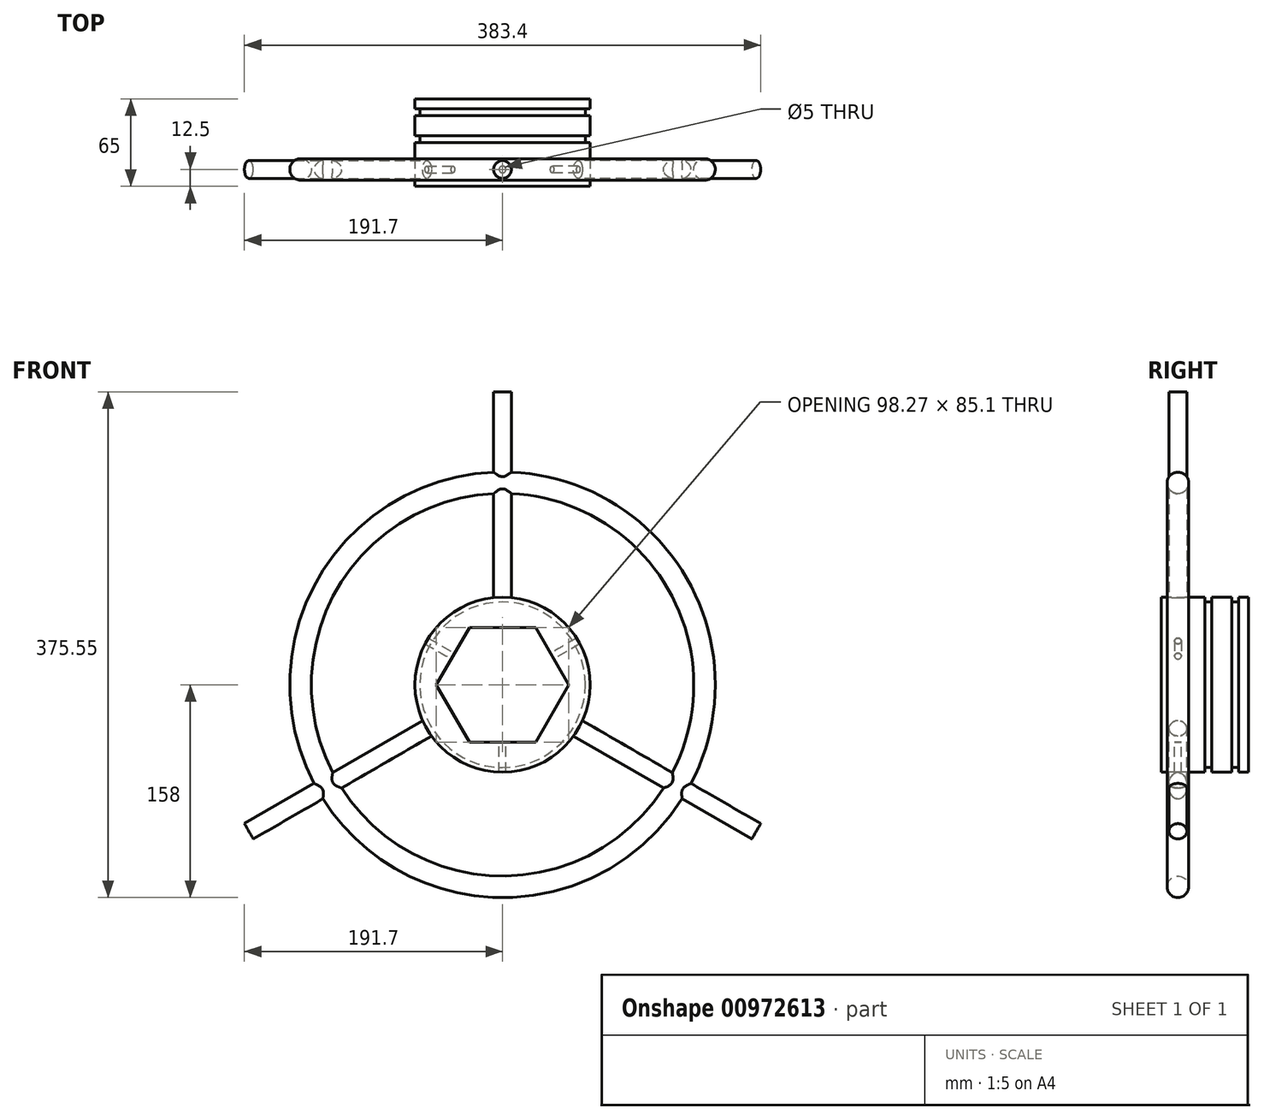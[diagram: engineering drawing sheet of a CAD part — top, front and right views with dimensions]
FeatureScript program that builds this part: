
annotation { "Feature Type Name" : "Feature", "Feature Type Description" : "" }
export const myFeature = defineFeature(function(context is Context, id is Id, definition is map)
    precondition{}
    {
        {
            var Q0;
            Q0=qCreatedBy(makeId("Front.planeOp"),FACE);
            var sketch = newSketch(context, id + "F0", { "sketchPlane" : qUnion([Q0])});
            skArc(sketch, "E0.cCircle", {"start": v(21.28, 36.85) * mm, "mid": v(-21.27, 36.85) * mm, "end": v(-42.55, 0) * mm, "construction": true});
            skLineSegment(sketch, "E0.0", {"start": v(-24.57, 42.55) * mm, "end": v(24.57, 42.55) * mm});
            skLineSegment(sketch, "E0.5", {"start": v(-49.13, 0) * mm, "end": v(-24.57, 42.55) * mm});
            skPoint(sketch, "E0.0.midPoint", {"position": v(0, 42.55) * mm});
            skArc(sketch, "E1", {"start": v(32.5, 56.3) * mm, "mid": v(-32.5, 56.3) * mm, "end": v(-65, 0) * mm});
            skLineSegment(sketch, "E2", {"start": v(24.57, 42.55) * mm, "end": v(0, 0) * mm});
            skLineSegment(sketch, "E3", {"start": v(-49.13, 0) * mm, "end": v(0, 0) * mm});
            skLineSegment(sketch, "E4", {"start": v(-49.13, 0) * mm, "end": v(-65, 0) * mm});
            skLineSegment(sketch, "E5", {"start": v(0, 0) * mm, "end": v(32.5, 56.3) * mm});
            skCircle(sketch, "E6", {"center": v(0, 0) * mm, "radius": 150 * mm});
            skSolve(sketch);
        }
        {
            var Q0;
            Q0=makeQuery(id+"F0.imprint","IMPRINT",FACE,{"disambiguationData":[TD([[makeQuery(id+"F0.imprint","IMPRINT",EDGE,{"derivedFrom":sQuery(id+"F0.wireOp",EDGE,"E0.0")}),1.0]])]});
            extrude(context, id + "F1", {"entities" : qUnion([Q0]), "oppositeDirection" : true, "depth" : 65 * mm, "offsetDistance" : 25 * mm});
        }
        {
            var Q0;
            Q0=makeQuery(id+"F1.opExtrude","SWEPT_FACE",FACE,{"disambiguationData":[OSD([sQuery(id+"F0.wireOp",EDGE,"E0.5")])]});
            var sketch = newSketch(context, id + "F2", { "sketchPlane" : qUnion([Q0])});
            skPoint(sketch, "E7", {"position": v(12.5, 0) * mm});
            skLineSegment(sketch, "E8.bottom", {"start": v(-10.68, 8.2) * mm, "end": v(-18.97, 8.2) * mm});
            skLineSegment(sketch, "E8.top", {"start": v(-10.68, 16.5) * mm, "end": v(-18.97, 16.5) * mm});
            skLineSegment(sketch, "E8.left", {"start": v(-10.68, 8.2) * mm, "end": v(-10.68, 16.5) * mm});
            skLineSegment(sketch, "E8.right", {"start": v(-18.97, 8.2) * mm, "end": v(-18.97, 16.5) * mm});
            skSolve(sketch);
        }
        {
            var Q0;
            Q0=sQuery(id+"F2.wireOp",VERTEX,"E7");
            var Q1;
            Q1=sQuery(id+"FKjmbhYk0okhU2k.wireOp",VERTEX,"e9ec7f22-f7e3-428d-b200-8865b6bfe14b");
            var Q2;
            Q2=sQuery(id+"FTpLO1T2TojNtAm.wireOp",VERTEX,"3d24cd9d-ed1b-48a1-b95c-8f817293be9f");
            var Q3;
            Q3=makeQuery(id+"F1.opExtrude","SWEPT_BODY",BODY,{"disambiguationData":[OSD([sQuery(id+"F0.wireOp",EDGE,"E0.0"),sQuery(id+"F0.wireOp",EDGE,"E0.1"),sQuery(id+"F0.wireOp",EDGE,"E0.2"),sQuery(id+"F0.wireOp",EDGE,"E0.3"),sQuery(id+"F0.wireOp",EDGE,"E0.4"),sQuery(id+"F0.wireOp",EDGE,"E0.5"),sQuery(id+"F0.wireOp",EDGE,"E1")])]});
            hole(context, id + "F3", {"style" : HoleStyle.SIMPLE, "endStyle" : HoleEndStyle.THROUGH, "standardTappedOrClearance" : lookupTablePath({ "standard" : "ISO", "engagement" : "75%", "pitch" : "1 mm", "size" : "M6", "type" : "Tapped" }), "standardBlindInLast" : lookupTablePath({ "standard" : "ISO", "fit" : "Normal", "engagement" : "75%", "pitch" : "1 mm", "size" : "M6", "type" : "Clearance & tapped" }), "holeDiameter" : 5 * mm, "majorDiameter" : 6 * mm, "showTappedDepth" : true, "isTappedThrough" : true, "tappedDepth" : 12 * mm, "tapClearance" : 3, "startFromSketch" : true, "locations" : qUnion([Q0, Q1, Q2]), "scope" : qUnion([Q3])});
        }
        {
            var Q0;
            Q0=makeQuery(id+"F1.opExtrude","SWEPT_FACE",FACE,{"disambiguationData":[OSD([sQuery(id+"F0.wireOp",EDGE,"E0.0")])]});
            var sketch = newSketch(context, id + "F4", { "sketchPlane" : qUnion([Q0])});
            skCircle(sketch, "E9", {"center": v(0, -12.5) * mm, "radius": 6.6 * mm});
            skSolve(sketch);
        }
        {
            var Q0;
            Q0=makeQuery(id+"F4.imprint","IMPRINT",FACE,{"disambiguationData":[TD([[makeQuery(id+"F4.imprint","IMPRINT",EDGE,{"derivedFrom":sQuery(id+"F4.wireOp",EDGE,"E9")}),1.0]])]});
            extrude(context, id + "F5", {"entities" : qUnion([Q0]), "oppositeDirection" : true, "depth" : 175 * mm, "offsetDistance" : 25 * mm});
        }
        {
            var Q0;
            Q0=makeQuery(id+"F5.opExtrude","SWEPT_BODY",BODY,{"disambiguationData":[OSD([sQuery(id+"F4.wireOp",EDGE,"E9")])]});
            var Q1;
            Q1=makeQuery(id+"F1.opExtrude","SWEPT_BODY",BODY,{"disambiguationData":[OSD([sQuery(id+"F0.wireOp",EDGE,"E0.0"),sQuery(id+"F0.wireOp",EDGE,"E0.5"),sQuery(id+"F0.wireOp",EDGE,"E1"),sQuery(id+"F0.wireOp",EDGE,"E4"),sQuery(id+"F0.wireOp",EDGE,"E5")])]});
            var Q2;
            Q2=makeQuery(id+"F1.opExtrude","CAP_EDGE",EDGE,{"disambiguationData":[OSD([sQuery(id+"F0.wireOp",EDGE,"E1")])],"isStart":true});
            circularPattern(context, id + "F6", {"operationType" : NewBodyOperationType.ADD, "entities" : qUnion([Q0, Q1]), "axis" : qUnion([Q2]), "angle" : 360 * degree, "instanceCount" : 3, "equalSpace" : true});
        }
        {
            var Q0;
            Q0=qCreatedBy(makeId("Right.planeOp"),FACE);
            var sketch = newSketch(context, id + "F7", { "sketchPlane" : qUnion([Q0])});
            skLineSegment(sketch, "E10.bottom", {"start": v(37.5, 67.56) * mm, "end": v(32.5, 67.56) * mm});
            skLineSegment(sketch, "E10.top", {"start": v(37.5, 61.44) * mm, "end": v(32.5, 61.44) * mm});
            skLineSegment(sketch, "E10.left", {"start": v(37.5, 67.56) * mm, "end": v(37.5, 61.44) * mm});
            skLineSegment(sketch, "E10.right", {"start": v(32.5, 67.56) * mm, "end": v(32.5, 61.44) * mm});
            skPoint(sketch, "E10.middle", {"position": v(35, 64.5) * mm});
            skLineSegment(sketch, "E11.bottom", {"start": v(57.5, 67.56) * mm, "end": v(52.5, 67.56) * mm});
            skLineSegment(sketch, "E11.top", {"start": v(57.5, 61.44) * mm, "end": v(52.5, 61.44) * mm});
            skLineSegment(sketch, "E11.left", {"start": v(57.5, 67.56) * mm, "end": v(57.5, 61.44) * mm});
            skLineSegment(sketch, "E11.right", {"start": v(52.5, 67.56) * mm, "end": v(52.5, 61.44) * mm});
            skPoint(sketch, "E11.middle", {"position": v(55, 64.5) * mm});
            skSolve(sketch);
        }
        {
            var Q0;
            Q0=makeQuery(id+"F7.imprint","IMPRINT",FACE,{"disambiguationData":[TD([[makeQuery(id+"F7.imprint","IMPRINT",EDGE,{"derivedFrom":sQuery(id+"F7.wireOp",EDGE,"E11.bottom")}),1.0]])]});
            var Q1;
            Q1=makeQuery(id+"F7.imprint","IMPRINT",FACE,{"disambiguationData":[TD([[makeQuery(id+"F7.imprint","IMPRINT",EDGE,{"derivedFrom":sQuery(id+"F7.wireOp",EDGE,"E10.bottom")}),1.0]])]});
            var Q2;
            Q2=makeQuery(id+"F1.opExtrude","CAP_EDGE",EDGE,{"disambiguationData":[OSD([sQuery(id+"F0.wireOp",EDGE,"E1")])],"isStart":false});
            revolve(context, id + "F8", {"operationType" : NewBodyOperationType.REMOVE, "surfaceOperationType" : NewSurfaceOperationType.NEW, "entities" : qUnion([Q0, Q1]), "axis" : qUnion([Q2]), "revolveType" : RevolveType.FULL, "oppositeDirection" : true});
        }
        {
            var Q0;
            Q0=qCreatedBy(makeId("Right.planeOp"),FACE);
            var sketch = newSketch(context, id + "F9", { "sketchPlane" : qUnion([Q0])});
            skCircle(sketch, "E12", {"center": v(12.5, 150) * mm, "radius": 8 * mm});
            skSolve(sketch);
        }
        {
            var Q0;
            Q0=makeQuery(id+"F9.imprint","IMPRINT",FACE,{"disambiguationData":[TD([[makeQuery(id+"F9.imprint","IMPRINT",EDGE,{"derivedFrom":sQuery(id+"F9.wireOp",EDGE,"E12")}),1.0]])]});
            var Q1;
            Q1=sQuery(id+"F0.wireOp",EDGE,"E6");
            revolve(context, id + "F10", {"operationType" : NewBodyOperationType.ADD, "surfaceOperationType" : NewSurfaceOperationType.NEW, "entities" : qUnion([Q0]), "axis" : qUnion([Q1]), "revolveType" : RevolveType.FULL});
        }
    });
